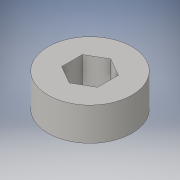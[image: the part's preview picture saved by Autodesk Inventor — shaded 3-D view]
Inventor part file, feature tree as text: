
AUTODESK INVENTOR PART (.ipt)
format: ipt  version: 2016 (Build 200138000, 138)  size: 95,232 bytes
history: native  units: in
note: dims shown in document units (in); Inventor stores cm internally (conversion verified against a paired STEP export)
features: extrude x1, sketch x1
ambient origin geometry x8: Origin, YZ Plane, XZ Plane, XY Plane, X Axis, Y Axis, Z Axis, Center Point
bodies: Solid1 (feature_tree)
feature tree (2):
  extrude  "Extrusion1"  Depth=0.375in
  sketch  "Sketch1"  dims[d0=0.875in d1=0.375in d2=0.345in d3=0.0in]
